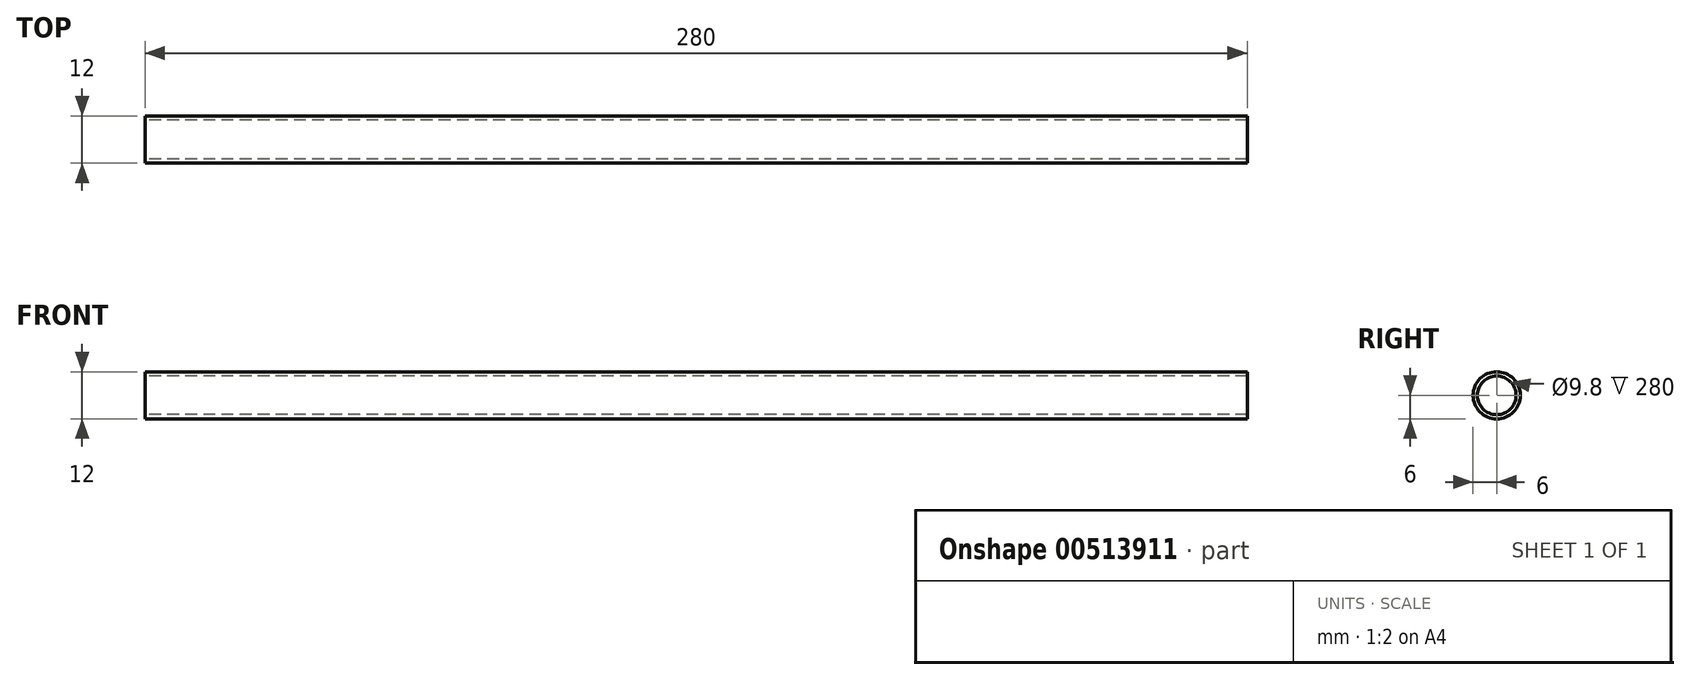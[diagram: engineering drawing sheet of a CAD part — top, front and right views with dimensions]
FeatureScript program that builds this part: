
annotation { "Feature Type Name" : "Feature", "Feature Type Description" : "" }
export const myFeature = defineFeature(function(context is Context, id is Id, definition is map)
    precondition{}
    {
        {
            var Q0;
            Q0=qCreatedBy(makeId("Right.planeOp"),FACE);
            var sketch = newSketch(context, id + "F0", { "sketchPlane" : qUnion([Q0])});
            skCircle(sketch, "E0", {"center": v(0, 0) * mm, "radius": 6 * mm});
            skCircle(sketch, "E1", {"center": v(0, 0) * mm, "radius": 4.9 * mm});
            skSolve(sketch);
        }
        {
            var Q0;
            Q0=makeQuery(id+"F0.imprint","IMPRINT",FACE,{"disambiguationData":[TD([[makeQuery(id+"F0.imprint","IMPRINT",EDGE,{"derivedFrom":sQuery(id+"F0.wireOp",EDGE,"E0")}),1.0]])]});
            extrude(context, id + "F1", {"entities" : qUnion([Q0]), "depth" : 280 * mm});
        }
    });
